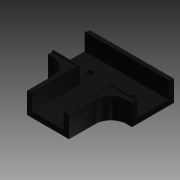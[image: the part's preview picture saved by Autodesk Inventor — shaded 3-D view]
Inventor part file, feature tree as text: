
AUTODESK INVENTOR PART (.ipt)
format: ipt  version: 2015 (Build 190159000, 159)  size: 190,464 bytes
history: native  units: in
note: dims shown in document units (in); Inventor stores cm internally (conversion verified against a paired STEP export)
features: extrude x6, sketch x6, other x3, split x1, fillet x1
ambient origin geometry x8: Origin, YZ Plane, XZ Plane, XY Plane, X Axis, Y Axis, Z Axis, Center Point
bodies: Solid1 (feature_tree)
feature tree (17):
  extrude  "Extrusion1"  Depth=1.0in
  extrude  "Extrusion2"  Depth=0.5in TaperAngle=0.0deg
  extrude  "Extrusion3"  Depth=0.5in
  extrude  "Extrusion4"  Depth=1.75in TaperAngle=0.0deg
  extrude  "Extrusion5"  Depth=0.75in
  split  "Split1"
  other  "Lip1"
  other  "Lip2"
  other  "Lip3"
  extrude  "Extrusion6"  Depth=0.375in
  fillet  "Fillet1"  Radius=1.0in
  sketch  "Sketch1"  dims[d0=1.0in d1=1.0in]
  sketch  "Sketch2"  dims[d2=2.0in d3=0.0in d4=0.5in d5=0.0in]
  sketch  "Sketch4"  dims[d6=0.5in d7=0.0in d8=0.75in]
  sketch  "Sketch5"  dims[d9=0.75in d10=1.75in d11=0.0in]
  sketch  "Sketch6"  dims[d12=0.75in d13=0.75in]
  sketch  "Sketch7"  dims[d14=1.75in d15=0.0in d16=0.03in d17=0.03in d18=0.0in d19=0.0in d20=0.0in d21=0.0in d22=0.03in d23=0.03in d24=0.0in d25=0.0in d26=0.0in d27=0.0in d28=0.03in d29=0.03in d30=0.0in d31=0.0in d32=0.0in d33=0.0in d34=0.141in d35=1.0in d36=0.0in d37=0.375in]
